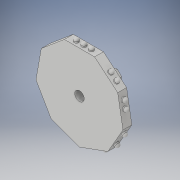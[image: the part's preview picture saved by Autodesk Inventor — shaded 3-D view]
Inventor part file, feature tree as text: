
AUTODESK INVENTOR PART (.ipt)
format: ipt  version: 2017 (Build 210142000, 142)  size: 303,104 bytes
history: native  units: in
note: dims shown in document units (in); Inventor stores cm internally (conversion verified against a paired STEP export)
features: extrude x5, sketch x5, pattern_circular x2, fillet x2
ambient origin geometry x8: Origin, YZ Plane, XZ Plane, XY Plane, X Axis, Y Axis, Z Axis, Center Point
bodies: Solid1 (feature_tree)
feature tree (14):
  extrude  "Extrusion1"  Depth=0.1181in TaperAngle=0.0deg
  extrude  "Extrusion2"  Depth=0.15in TaperAngle=0.0deg
  pattern_circular  "Circular Pattern1"  Count=8 Angle=360.0deg
  extrude  "Extrusion3"  TaperAngle=0.0deg  [1 undecoded]
  fillet  "Fillet1"  Radius=0.201in
  extrude  "Extrusion4"  Depth=0.0315in
  pattern_circular  "Circular Pattern2"  [2 undecoded]
  extrude  "Extrusion5"  Depth=0.0315in TaperAngle=360.0deg
  fillet  "Fillet2"  [1 undecoded]
  sketch  "Sketch1"  dims[d0=1.141in d1=0.1181in d2=0.0in]
  sketch  "Sketch2"  dims[d4=12.5984in d5=0.6in d6=360.0deg d7=0.04in d8=0.04in d9=0.075in d10=0.15in d11=0.0in d12=3.1496in d13=360.0deg]
  sketch  "Sketch3"  dims[d15=0.063in d16=0.1in d17=0.1in d18=0.063in d19=0.063in d20=0.0575in d21=0.059in d22=0.0in d23=0.059in d24=0.059in d25=0.236in d27=0.0in d28=0.201in]
  sketch  "Sketch4"  dims[d29=0.0472in d30=0.0in d31=0.0315in]
  sketch  "Sketch5"  dims[d32=0.126in d33=0.0472in d34=0.0in d35=3.5433in d36=360.0deg d38=0.0in d39=0.0in d40=0.0315in]
note: 4 required parameter values undecoded (feature->parameter linkage not recoverable at this tier; creation-order binding heuristic only, values carry confidence <= 0.55)
